# Revit family: QF_ELECTROLUXPROFESSIONAL_1LSNST_TD6-37_G
name_source: partatom
category: Attrezzature speciali
units: mm (PartAtom-declared; Revit-internal decimal feet)

## family parameters
Basato su piano di lavoro = No
Condiviso = No
Punto di calcolo locali = No
Quota connettore circolare = Usa diametro
Sempre verticale = Sì
Taglio con vuoti quando caricato = No
Tipo di parte = Normale

## types (28) — shared parameters
Depth Actual = 1560 mm  [stored 5.11811 ft]
Height Actual = 1855 mm  [stored 6.08596 ft]
Latent Heat Output = 0.0
Length Actual = 960 mm  [stored 3.14961 ft]
Modello = TD6-37
Produttore = Electrolux Professional
Sensible Heat Output = 0.0
URL = www.electroluxprofessional.com
Weight = 283
zero-valued in all types: Prospetto di default, Steam Pounds per Hour

## per-type parameters (varying)
| type | Cycle | Descrizione | Gas KW | Item Number | Phase | Volts | Watts |
| 9873030109 | 50 Hz | TUMBLE DRYER TD6-37 37KG SST DRUM GPL 42KW 200/50/3 COMPASS PRO 6L85 SST/SLVR DO.RIGHT REV DISCON DMPR | 0 | 1L0H9N | 3 | 200 V | 1500 W |
| 9873030050 | 50 Hz | TUMBLE DRYER TD6-37 37KG SST DRUM GAS 42KW 240/50/1 COMPASS PRO 6G82 SST/SLVR DO.RIGHT REV DISCON DMPR | 42 | 1LA1BA | 1 | 240 V | 1700 W |
| 9873030106 | 60 Hz | TUMBLE DRYER TD6-37 37KG GALVA.DRUM GAS 42KW 230/60/3 COMPASS PRO 6G82 SLVR/SLVR DO.LEFT REV DISCON DMPR | 0 | 1L0H8G | 3 | 230 V | 1500 W |
| 9873030097 | 50 Hz | TUMBLE DRYER TD6-37 37KG GALVA.DRUM GAS 42KW 380-415/50/3N COMPASS PRO 6G81 SLVR/SLVR DO.RIGHT REV MB DISCON DMPR | 0 | 1L0H24 | 3 | 415 V | 1500 W |
| 9873030008 | 50 Hz | TUMBLE DRYER TD6-37 37KG SST DRUM GAS 42KW 380-415/50/3N COMPASS PRO 6G81 SLVR/SLVR DO.RIGHT REV MB DISCON DMPR | 42 | 1L0G62 | 3 | 415 V | 1500 W |
| 9873030068 | 50 Hz | TUMBLE DRYER TD6-37 37KG GALVA.DRUM GAS 42KW 240/50/1 COMPASS PRO 6L80 2.I/O SLVR/SLVR DO.RIGHT ELS-NETW. REV DMPR | 42 | 1LA222 | 1 | 240 V | 1700 W |
| 9873030092 | 50 Hz | TUMBLE DRYER TD6-37 37KG GALVA.DRUM GAS 42KW 240/50/1 COMPASS PRO 6G82 SLVR/SLVR DO.RIGHT REV STOP DISCON DMPR | 42 | 1L828T | 1 | 240 V | 1700 W |
| 9873030057 | 50 Hz | TUMBLE DRYER TD6-37 37KG GALVA.DRUM GAS 42KW 380-415/50/3N COMPASS PRO 6G81 SLVR/SLVR DO.RIGHT REV MB STOP DISCON DMPR | 42 | 1LA1DF | 3 | 415 V | 1500 W |
| 9873030047 | 50 Hz | TUMBLE DRYER TD6-37 37KG SST DRUM GAS 42KW 380-415/50/3N COMPASS PRO 6G81 SST/SLVR DO.RIGHT REV MB STOP DISCON DMPR | 42 | 1L0GCN | 3 | 415 V | 1500 W |
| 9873030002 | 50 Hz | TUMBLE DRYER TD6-37 37KG GALVA.DRUM GAS 42KW 380-415/50/3N COMPASS PRO 6G81 SLVR/SLVR DO.RIGHT REV MB STOP DISCON DMPR | 42 | 1L0G3V | 3 | 415 V | 1500 W |
| 9873030072 | 50 Hz | TUMBLE DRYER TD6-37 37KG SST DRUM GAS 42KW 230/50/1 COMPASS PRO 6G81 SLVR/SLVR DO.RIGHT REV MB STOP DISCON DMPR | 42 | 1L999S | 1 | 230 V | 1700 W |
| 9873030110 | 60 Hz | TUMBLE DRYER TD6-37 37KG SST DRUM GPL 42KW 200/60/3 COMPASS PRO 6L85 SST/SLVR DO.RIGHT REV DISCON DMPR | 42 | 1L0H9P | 3 | 200 V | 1500 W |
| 9873030100 | 60 Hz | TUMBLE DRYER TD6-37 37KG SST DRUM GPL 42KW 200/60/3 COMPASS PRO 6G86 SLVR/SLVR DO.RIGHT REV DISCON DMPR | 0 | 1LT5ZC | 3 | 200 V | 1500 W |
| 9873030108 | 60 Hz | TUMBLE DRYER TD6-37 37KG SST DRUM GPL 42KW 200/60/3 COMPASS PRO 6L85 SLVR/SLVR DO.RIGHT REV DISCON DMPR | 0 | 1L0H98 | 3 | 200 V | 1500 W |
| 9873030021 | 50 Hz | TUMBLE DRYER TD6-37 37KG GALVA.DRUM GAS 42KW 380-415/50/3N COMPASS PRO 6G82 SLVR/SLVR DO.RIGHT REV STOP DISCON DMPR | 42 | 1L0G6F | 3 | 415 V | 1500 W |
| 9873030011 | 50 Hz | TUMBLE DRYER TD6-37 37KG GALVA.DRUM GAS 42KW 380-415/50/3N COMPASS PRO 6G82 SLVR/SLVR DO.RIGHT REV DISCON DMPR | 42 | 1L0G65 | 3 | 415 V | 1500 W |
| 9873030061 | 50 Hz | TUMBLE DRYER TD6-37 37KG GALVA.DRUM GAS 42KW 230/50/3 COMPASS PRO 6G81 SLVR/SLVR DO.RIGHT REV MB STOP DISCON DMPR | 42 | 1L0GDK | 3 | 230 V | 1500 W |
| 9873030041 | 50 Hz | TUMBLE DRYER TD6-37 37KG SST DRUM GAS 42KW 380-415/50/3N COMPASS PRO 6G82 SLVR/SLVR DO.LEFT REV STOP DISCON DMPR | 42 | 1LSP55 | 3 | 415 V | 1500 W |
| 9873030059 | 50 Hz | TUMBLE DRYER TD6-37 37KG SST DRUM GAS 42KW 380-415/50/3N COMPASS PRO 6G81 SLVR/SLVR DO.RIGHT REV MB STOP DISCON DMPR | 42 | 1L0GDD | 3 | 415 V | 1500 W |
| 9873030049 | 50 Hz | TUMBLE DRYER TD6-37 37KG GALVA.DRUM GAS 42KW 240/50/1 COMPASS PRO 6G81 SLVR/SLVR DO.RIGHT REV MB STOP DISCON DMPR | 42 | 1L0GD9 | 1 | 240 V | 1700 W |
| 9873030102 | 50 Hz | TUMBLE DRYER TD6-37 37KG SST DRUM GPL 42KW 200/50/3 COMPASS PRO 6G86 SLVR/SLVR DO.RIGHT REV DISCON DMPR | 0 | 1LT5ZD | 3 | 200 V | 1500 W |
| 9873030064 | 60 Hz | TUMBLE DRYER TD6-37 37KG GALVA.DRUM GAS 42KW 220/60/1 COMPASS PRO 6G82 SLVR/SLVR DO.RIGHT REV DISCON DMPR | 42 | 1L0GG2 | 1 | 220 V | 1700 W |
| 9873030054 | 50 Hz | TUMBLE DRYER TD6-37 37KG SST DRUM GAS 42KW 380-415/50/3N COMPASS PRO 6G82 SLVR/SLVR DO.RIGHT REV STOP DISCON DMPR | 42 | 1LA1BY | 3 | 415 V | 1500 W |
| 9873030013 | 60 Hz | TUMBLE DRYER TD6-37 37KG GALVA.DRUM GAS 42KW 230/60/3 COMPASS PRO 6G82 SLVR/SLVR DO.RIGHT REV DISCON DMPR | 42 | 1L0G67 | 3 | 230 V | 1500 W |
| 9873030003 | 50 Hz | TUMBLE DRYER TD6-37 37KG GALVA.DRUM GAS 42KW 240/50/1 COMPASS PRO 6G81 SLVR/SLVR DO.RIGHT REV MB STOP DISCON DMPR | 42 | 1L0G5X | 1 | 240 V | 1700 W |
| 9873030107 | 50 Hz | TUMBLE DRYER TD6-37 37KG SST DRUM GPL 42KW 200/50/3 COMPASS PRO 6L85 SLVR/SLVR DO.RIGHT REV DISCON DMPR | 0 | 1L0H97 | 3 | 200 V | 1500 W |
| 9873030114 | 60 Hz | TUMBLE DRYER TD6-37 37KG GALVA.DRUM GAS 42KW 220/60/3 COMPASS PRO 6G82 SLVR/SLVR DO.LEFT REV DISCON DMPR | 0 | 1LT65M | 3 | 220 V | 1500 W |
| 9873030005 | 50 Hz | TUMBLE DRYER TD6-37 37KG GALVA.DRUM GAS 42KW 380-415/50/3N COMPASS PRO 6G82 SLVR/SLVR DO.RIGHT REV DMPR | 42 | 1L0G5Z | 3 | 415 V | 1500 W |

note: [stored X ft] marks values corroborated as IEEE doubles in the binary element streams (Revit-internal decimal feet)

## geometry (parser evidence)
native form markers: Blend x8
no freeform markers — native parametric forms only
